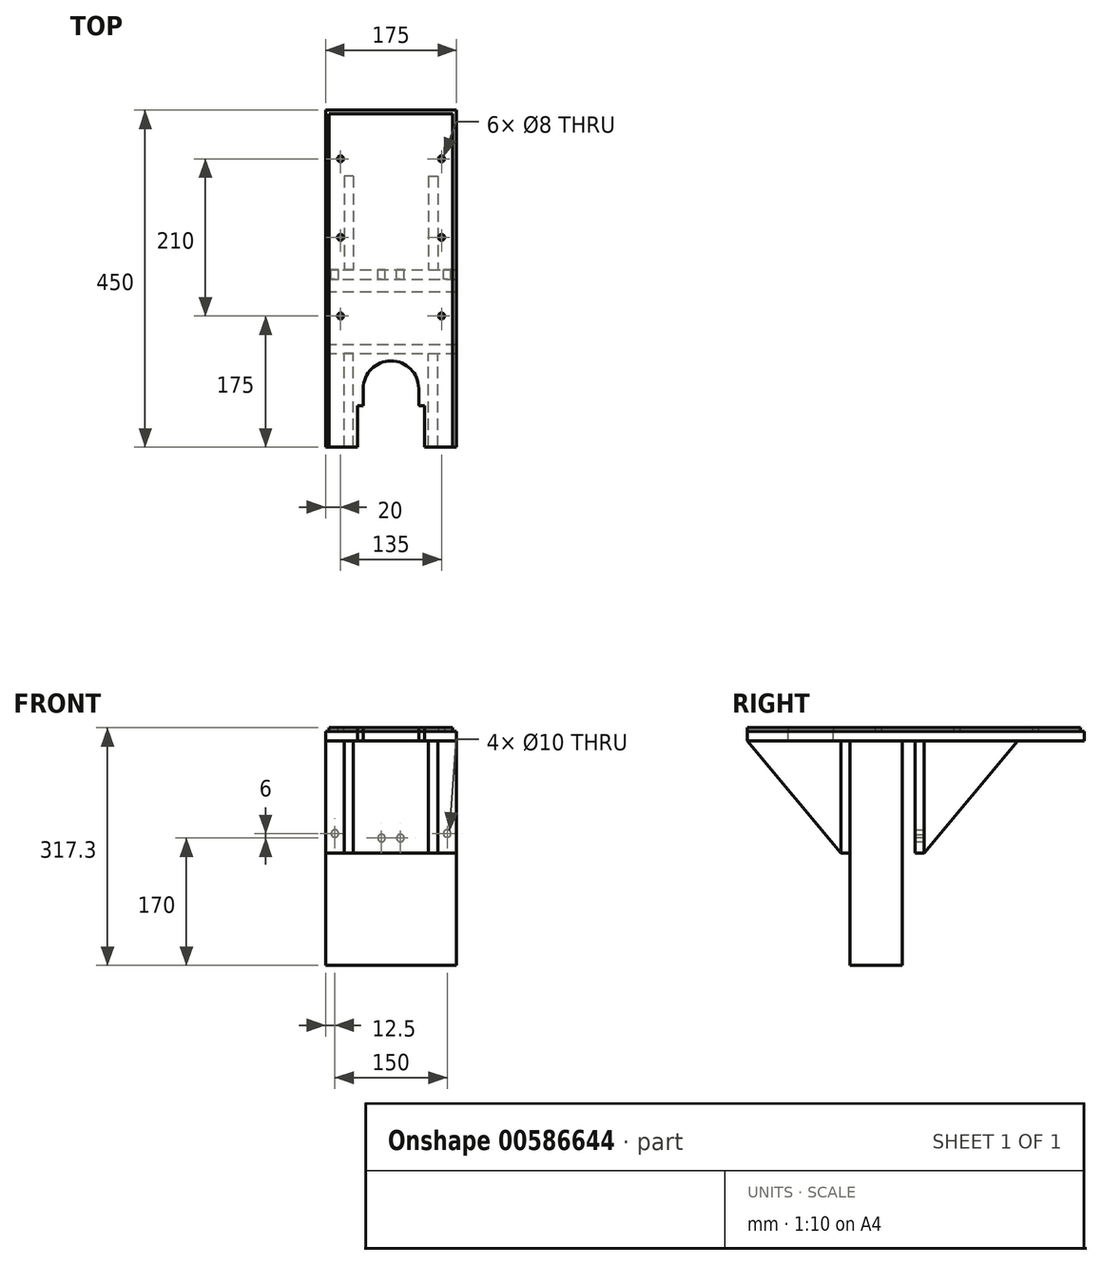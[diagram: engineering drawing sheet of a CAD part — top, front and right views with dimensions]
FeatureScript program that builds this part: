
annotation { "Feature Type Name" : "Feature", "Feature Type Description" : "" }
export const myFeature = defineFeature(function(context is Context, id is Id, definition is map)
    precondition{}
    {
        {
            assignVariable(context, id + "F0", {"name" : "woodThickness", "anyValue" : 12.3});
        }
        {
            var Q0;
            Q0=qCreatedBy(makeId("Top.planeOp"),FACE);
            var sketch = newSketch(context, id + "F1", { "sketchPlane" : qUnion([Q0])});
            skLineSegment(sketch, "E0.bottom", {"start": v(-82.5, 0) * mm, "end": v(82.5, 0) * mm});
            skLineSegment(sketch, "E0.top", {"start": v(-82.5, -445) * mm, "end": v(-45, -445) * mm});
            skLineSegment(sketch, "E0.left", {"start": v(-82.5, 0) * mm, "end": v(-82.5, -445) * mm});
            skLineSegment(sketch, "E0.right", {"start": v(82.5, 0) * mm, "end": v(82.5, -445) * mm});
            skPoint(sketch, "E1", {"position": v(0, 0) * mm});
            skCircle(sketch, "E2", {"center": v(-67.5, -60) * mm, "radius": 4 * mm});
            skCircle(sketch, "E3", {"center": v(-67.5, -165) * mm, "radius": 4 * mm});
            skCircle(sketch, "E4", {"center": v(-67.5, -270) * mm, "radius": 4 * mm});
            skCircle(sketch, "E5.MirrorC", {"center": v(67.5, -60) * mm, "radius": 4 * mm});
            skCircle(sketch, "E6.MirrorC", {"center": v(67.5, -165) * mm, "radius": 4 * mm});
            skCircle(sketch, "E7.MirrorC", {"center": v(67.5, -270) * mm, "radius": 4 * mm});
            skLineSegment(sketch, "E8", {"start": v(-67.5, -60) * mm, "end": v(-67.5, -320.53) * mm, "construction": true});
            skArc(sketch, "E9", {"start": v(37, -367) * mm, "mid": v(0, -330) * mm, "end": v(-37, -367) * mm});
            skLineSegment(sketch, "E10", {"start": v(-45, -445) * mm, "end": v(-45, -390) * mm});
            skLineSegment(sketch, "E11.MirrorCS", {"start": v(45, -445) * mm, "end": v(45, -390) * mm});
            skLineSegment(sketch, "E12", {"start": v(-45, -390) * mm, "end": v(-37, -390) * mm});
            skLineSegment(sketch, "E13", {"start": v(-37, -390) * mm, "end": v(-37, -367) * mm});
            skLineSegment(sketch, "E14.MirrorCS", {"start": v(37, -390) * mm, "end": v(37, -367) * mm});
            skLineSegment(sketch, "E15.MirrorCS", {"start": v(45, -390) * mm, "end": v(37, -390) * mm});
            skPoint(sketch, "E16.orphan", {"position": v(-37, -348.16) * mm});
            skPoint(sketch, "E17.orphan", {"position": v(37, -348.16) * mm});
            skLineSegment(sketch, "E18.trimOffspring", {"start": v(45, -445) * mm, "end": v(82.5, -445) * mm});
            skSolve(sketch);
        }
        {
            var Q0;
            Q0=makeQuery(id+"F1.imprint","IMPRINT",FACE,{"disambiguationData":[TD([[makeQuery(id+"F1.imprint","IMPRINT",EDGE,{"derivedFrom":sQuery(id+"F1.wireOp",EDGE,"E0.bottom")}),-1.0]])]});
            extrude(context, id + "F2", {"entities" : qUnion([Q0]), "depth" : 5 * mm, "offsetDistance" : 25 * mm});
        }
        {
            var Q0;
            Q0=makeQuery(id+"F2.opExtrude","CAP_FACE",FACE,{"disambiguationData":[OSD([sQuery(id+"F1.wireOp",EDGE,"E0.bottom"),sQuery(id+"F1.wireOp",EDGE,"E0.top"),sQuery(id+"F1.wireOp",EDGE,"E0.left"),sQuery(id+"F1.wireOp",EDGE,"E0.right"),sQuery(id+"F1.wireOp",EDGE,"E2"),sQuery(id+"F1.wireOp",EDGE,"E3"),sQuery(id+"F1.wireOp",EDGE,"E4"),sQuery(id+"F1.wireOp",EDGE,"E5.MirrorC"),sQuery(id+"F1.wireOp",EDGE,"E6.MirrorC"),sQuery(id+"F1.wireOp",EDGE,"E7.MirrorC"),sQuery(id+"F1.wireOp",EDGE,"E9"),sQuery(id+"F1.wireOp",EDGE,"E10"),sQuery(id+"F1.wireOp",EDGE,"E11.MirrorCS"),sQuery(id+"F1.wireOp",EDGE,"E12"),sQuery(id+"F1.wireOp",EDGE,"E13"),sQuery(id+"F1.wireOp",EDGE,"E14.MirrorCS"),sQuery(id+"F1.wireOp",EDGE,"E15.MirrorCS"),sQuery(id+"F1.wireOp",EDGE,"E18.trimOffspring")])],"isStart":true});
            var sketch = newSketch(context, id + "F3", { "sketchPlane" : qUnion([Q0])});
            skLineSegment(sketch, "E19.bottom", {"start": v(-87.5, -5) * mm, "end": v(87.5, -5) * mm});
            skLineSegment(sketch, "E19.top", {"start": v(-87.5, 445) * mm, "end": v(-45, 445) * mm});
            skLineSegment(sketch, "E19.left", {"start": v(-87.5, -5) * mm, "end": v(-87.5, 445) * mm});
            skLineSegment(sketch, "E19.right", {"start": v(87.5, -5) * mm, "end": v(87.5, 445) * mm});
            skArc(sketch, "E20", {"start": v(-37, 367) * mm, "mid": v(0, 330) * mm, "end": v(37, 367) * mm});
            skArc(sketch, "E21.0", {"start": v(37, 367) * mm, "mid": v(0, 330) * mm, "end": v(-37, 367) * mm});
            skLineSegment(sketch, "E22", {"start": v(-37, 367) * mm, "end": v(-37, 390) * mm});
            skLineSegment(sketch, "E23", {"start": v(-37, 390) * mm, "end": v(-45, 390) * mm});
            skLineSegment(sketch, "E24", {"start": v(-45, 390) * mm, "end": v(-45, 445) * mm});
            skLineSegment(sketch, "E25.MirrorCS", {"start": v(37, 367) * mm, "end": v(37, 390) * mm});
            skLineSegment(sketch, "E26.MirrorCS", {"start": v(37, 390) * mm, "end": v(45, 390) * mm});
            skLineSegment(sketch, "E27.MirrorCS", {"start": v(45, 390) * mm, "end": v(45, 445) * mm});
            skLineSegment(sketch, "E28.trimOffspring", {"start": v(45, 445) * mm, "end": v(87.5, 445) * mm});
            skSolve(sketch);
        }
        {
            var Q0;
            Q0 = qSketchRegion(id + "F3", true);
            extrude(context, id + "F4", {"entities" : qUnion([Q0]), "depth" : (getVariable(context, 'woodThickness')) * mm, "offsetDistance" : 25 * mm});
        }
        {
            var Q0;
            Q0=makeQuery(id+"F4.opExtrude","CAP_FACE",FACE,{"disambiguationData":[OSD([sQuery(id+"F3.wireOp",EDGE,"E19.bottom"),sQuery(id+"F3.wireOp",EDGE,"E19.top"),sQuery(id+"F3.wireOp",EDGE,"E19.left"),sQuery(id+"F3.wireOp",EDGE,"E19.right")])],"isStart":false});
            var sketch = newSketch(context, id + "F5", { "sketchPlane" : qUnion([Q0])});
            skLineSegment(sketch, "E29.bottom", {"start": v(-87.5, 237.7) * mm, "end": v(87.5, 237.7) * mm});
            skLineSegment(sketch, "E29.top", {"start": v(-87.5, 307.7) * mm, "end": v(87.5, 307.7) * mm});
            skLineSegment(sketch, "E29.left", {"start": v(-87.5, 237.7) * mm, "end": v(-87.5, 307.7) * mm});
            skLineSegment(sketch, "E29.right", {"start": v(87.5, 237.7) * mm, "end": v(87.5, 307.7) * mm});
            skPoint(sketch, "E30", {"position": v(0, 237.7) * mm});
            skSolve(sketch);
        }
        {
            var Q0;
            Q0 = qSketchRegion(id + "F5", true);
            extrude(context, id + "F6", {"entities" : qUnion([Q0]), "depth" : 300 * mm, "offsetDistance" : 25 * mm});
        }
        {
            var Q0;
            {var subQ6=makeQuery(id+"F4.opExtrude","CAP_EDGE",EDGE,{"disambiguationData":[OSD([sQuery(id+"F3.wireOp",EDGE,"E19.top")])],"isStart":false});Q0=makeQuery(id+"F5.imprint","IMPRINT",FACE,{"disambiguationData":[TD([[makeQuery(id+"F5.imprint","IMPRINT",EDGE,{"derivedFrom":subQ6}),-1.0]])]});}
            var sketch = newSketch(context, id + "F7", { "sketchPlane" : qUnion([Q0])});
            skLineSegment(sketch, "E31.bottom", {"start": v(-87.5, 320) * mm, "end": v(87.5, 320) * mm});
            skLineSegment(sketch, "E31.top", {"start": v(-87.5, 307.7) * mm, "end": v(87.5, 307.7) * mm});
            skLineSegment(sketch, "E31.left", {"start": v(-87.5, 320) * mm, "end": v(-87.5, 307.7) * mm});
            skLineSegment(sketch, "E31.right", {"start": v(87.5, 320) * mm, "end": v(87.5, 307.7) * mm});
            skPoint(sketch, "E32", {"position": v(-97.13, 272.7) * mm});
            skLineSegment(sketch, "E33.MirrorCS", {"start": v(-87.5, 208.4) * mm, "end": v(-87.5, 220.7) * mm});
            skLineSegment(sketch, "E34.MirrorCS", {"start": v(-87.5, 220.7) * mm, "end": v(87.5, 220.7) * mm});
            skLineSegment(sketch, "E35.MirrorCS", {"start": v(-87.5, 208.4) * mm, "end": v(87.5, 208.4) * mm});
            skLineSegment(sketch, "E36.MirrorCS", {"start": v(87.5, 208.4) * mm, "end": v(87.5, 220.7) * mm});
            skLineSegment(sketch, "E37.bottom", {"start": v(-57.94, 220.7) * mm, "end": v(-44.03, 220.7) * mm, "construction": true});
            skLineSegment(sketch, "E37.top", {"start": v(-57.94, 225.7) * mm, "end": v(-44.03, 225.7) * mm, "construction": true});
            skLineSegment(sketch, "E37.left", {"start": v(-57.94, 220.7) * mm, "end": v(-57.94, 225.7) * mm, "construction": true});
            skLineSegment(sketch, "E37.right", {"start": v(-44.03, 220.7) * mm, "end": v(-44.03, 225.7) * mm, "construction": true});
            skLineSegment(sketch, "E38.bottom", {"start": v(-35.87, 225.7) * mm, "end": v(-63.84, 225.7) * mm, "construction": true});
            skLineSegment(sketch, "E38.top", {"start": v(-35.87, 237.7) * mm, "end": v(-63.84, 237.7) * mm, "construction": true});
            skLineSegment(sketch, "E38.left", {"start": v(-35.87, 225.7) * mm, "end": v(-35.87, 237.7) * mm, "construction": true});
            skLineSegment(sketch, "E38.right", {"start": v(-63.84, 225.7) * mm, "end": v(-63.84, 237.7) * mm, "construction": true});
            skSolve(sketch);
        }
        {
            var Q0;
            Q0 = qSketchRegion(id + "F7", true);
            extrude(context, id + "F8", {"entities" : qUnion([Q0]), "depth" : 150 * mm, "offsetDistance" : 25 * mm});
        }
        {
            var Q0;
            Q0=makeQuery(id+"F4.opExtrude","SWEPT_FACE",FACE,{"disambiguationData":[OSD([sQuery(id+"F3.wireOp",EDGE,"E19.left")])]});
            cPlane(context, id + "F9", {"entities" : qUnion([Q0]), "cplaneType" : CPlaneType.OFFSET, "offset" : 25 * mm, "oppositeDirection" : true, "width" : 150 * mm, "height" : 150 * mm});
        }
        {
            var Q0;
            Q0=qCreatedBy(id+"F9.planeOp",FACE);
            var sketch = newSketch(context, id + "F10", { "sketchPlane" : qUnion([Q0])});
            skLineSegment(sketch, "E39", {"start": v(445, -12.3) * mm, "end": v(320, -162.3) * mm});
            skLineSegment(sketch, "E40", {"start": v(320, -162.3) * mm, "end": v(320, -12.3) * mm});
            skLineSegment(sketch, "E41", {"start": v(320, -12.3) * mm, "end": v(445, -12.3) * mm});
            skLineSegment(sketch, "E42", {"start": v(208.4, -162.3) * mm, "end": v(208.4, -12.3) * mm});
            skLineSegment(sketch, "E43", {"start": v(208.4, -12.3) * mm, "end": v(83.4, -12.3) * mm});
            skLineSegment(sketch, "E44", {"start": v(83.4, -12.3) * mm, "end": v(208.4, -162.3) * mm});
            skSolve(sketch);
        }
        {
            var Q0;
            Q0 = qSketchRegion(id + "F10", true);
            extrude(context, id + "F11", {"entities" : qUnion([Q0]), "oppositeDirection" : true, "depth" : (getVariable(context, 'woodThickness')) * mm, "offsetDistance" : 25 * mm});
        }
        {
            var Q0;
            Q0=makeQuery(id+"F11.opExtrude","SWEPT_BODY",BODY,{"disambiguationData":[OSD([sQuery(id+"F10.wireOp",EDGE,"E42"),sQuery(id+"F10.wireOp",EDGE,"E43"),sQuery(id+"F10.wireOp",EDGE,"E44")])]});
            var Q1;
            Q1=makeQuery(id+"F11.opExtrude","SWEPT_BODY",BODY,{"disambiguationData":[OSD([sQuery(id+"F10.wireOp",EDGE,"E39"),sQuery(id+"F10.wireOp",EDGE,"E40"),sQuery(id+"F10.wireOp",EDGE,"E41")])]});
            var Q2;
            Q2=qCreatedBy(makeId("Right.planeOp"),FACE);
            mirror(context, id + "F12", {"entities" : qUnion([Q0, Q1]), "mirrorPlane" : qUnion([Q2])});
        }
        {
            var Q0;
            Q0=makeQuery(id+"F8.opExtrude","SWEPT_FACE",FACE,{"disambiguationData":[OSD([sQuery(id+"F7.wireOp",EDGE,"E35.MirrorCS")])]});
            var sketch = newSketch(context, id + "F13", { "sketchPlane" : qUnion([Q0])});
            skCircle(sketch, "E45", {"center": v(-12.6, -142.3) * mm, "radius": 5 * mm});
            skPoint(sketch, "E46", {"position": v(0, -177.73) * mm});
            skLineSegment(sketch, "E47", {"start": v(0, -177.73) * mm, "end": v(0, 117.83) * mm, "construction": true});
            skCircle(sketch, "E48", {"center": v(12.6, -142.3) * mm, "radius": 5 * mm});
            skLineSegment(sketch, "E49", {"start": v(50.2, -142.3) * mm, "end": v(12.6, -142.3) * mm, "construction": true});
            skLineSegment(sketch, "E50", {"start": v(-12.6, -142.3) * mm, "end": v(-50.2, -142.3) * mm, "construction": true});
            skLineSegment(sketch, "E51", {"start": v(-12.6, -142.3) * mm, "end": v(0, -177.73) * mm, "construction": true});
            skLineSegment(sketch, "E52", {"start": v(-50.2, -142.3) * mm, "end": v(50.2, -142.3) * mm, "construction": true});
            skPoint(sketch, "E53", {"position": v(0, -142.3) * mm});
            skLineSegment(sketch, "E54", {"start": v(0, -177.73) * mm, "end": v(12.6, -142.3) * mm, "construction": true});
            skCircle(sketch, "E55", {"center": v(12.6, -142.3) * mm, "radius": 21 * mm, "construction": true});
            skCircle(sketch, "E56", {"center": v(-12.6, -142.3) * mm, "radius": 21 * mm, "construction": true});
            skSolve(sketch);
        }
        {
            var Q0;
            Q0 = qSketchRegion(id + "F13", true);
            extrude(context, id + "F14", {"entities" : qUnion([Q0]), "operationType" : NewBodyOperationType.REMOVE, "endBound" : BoundingType.UP_TO_NEXT, "oppositeDirection" : true, "depth" : 25 * mm, "offsetDistance" : 25 * mm});
        }
        {
            var Q0;
            Q0=makeQuery(id+"F8.opExtrude","SWEPT_FACE",FACE,{"disambiguationData":[OSD([sQuery(id+"F7.wireOp",EDGE,"E35.MirrorCS")])]});
            var sketch = newSketch(context, id + "F15", { "sketchPlane" : qUnion([Q0])});
            skLineSegment(sketch, "E57.bottom", {"start": v(50.2, -136.3) * mm, "end": v(-50.2, -136.3) * mm, "construction": true});
            skLineSegment(sketch, "E57.top", {"start": v(50.2, -12.3) * mm, "end": v(-50.2, -12.3) * mm, "construction": true});
            skLineSegment(sketch, "E57.left", {"start": v(50.2, -136.3) * mm, "end": v(50.2, -12.3) * mm, "construction": true});
            skLineSegment(sketch, "E57.right", {"start": v(-50.2, -136.3) * mm, "end": v(-50.2, -12.3) * mm, "construction": true});
            skCircle(sketch, "E58", {"center": v(75, -136.3) * mm, "radius": 5 * mm});
            skCircle(sketch, "E59", {"center": v(-75, -136.3) * mm, "radius": 5 * mm});
            skCircle(sketch, "E60", {"center": v(75, -136.3) * mm, "radius": 21 * mm, "construction": true});
            skCircle(sketch, "E61", {"center": v(-75, -136.3) * mm, "radius": 21 * mm, "construction": true});
            skPoint(sketch, "E62", {"position": v(0, -136.3) * mm});
            skLineSegment(sketch, "E63", {"start": v(75, -136.3) * mm, "end": v(0, -136.3) * mm, "construction": true});
            skLineSegment(sketch, "E64", {"start": v(-75, -136.3) * mm, "end": v(0, -136.3) * mm, "construction": true});
            skLineSegment(sketch, "E65", {"start": v(50.2, -157.3) * mm, "end": v(-50.2, -157.3) * mm, "construction": true});
            skSolve(sketch);
        }
        {
            var Q0;
            Q0 = qSketchRegion(id + "F15", true);
            var Q1;
            Q1=makeQuery(id+"F8.opExtrude","SWEPT_FACE",FACE,{"disambiguationData":[OSD([sQuery(id+"F7.wireOp",EDGE,"E34.MirrorCS")])]});
            extrude(context, id + "F16", {"entities" : qUnion([Q0]), "operationType" : NewBodyOperationType.REMOVE, "endBound" : BoundingType.UP_TO_SURFACE, "oppositeDirection" : true, "depth" : 25 * mm, "endBoundEntityFace" : qUnion([Q1]), "offsetDistance" : 25 * mm});
        }
    });
